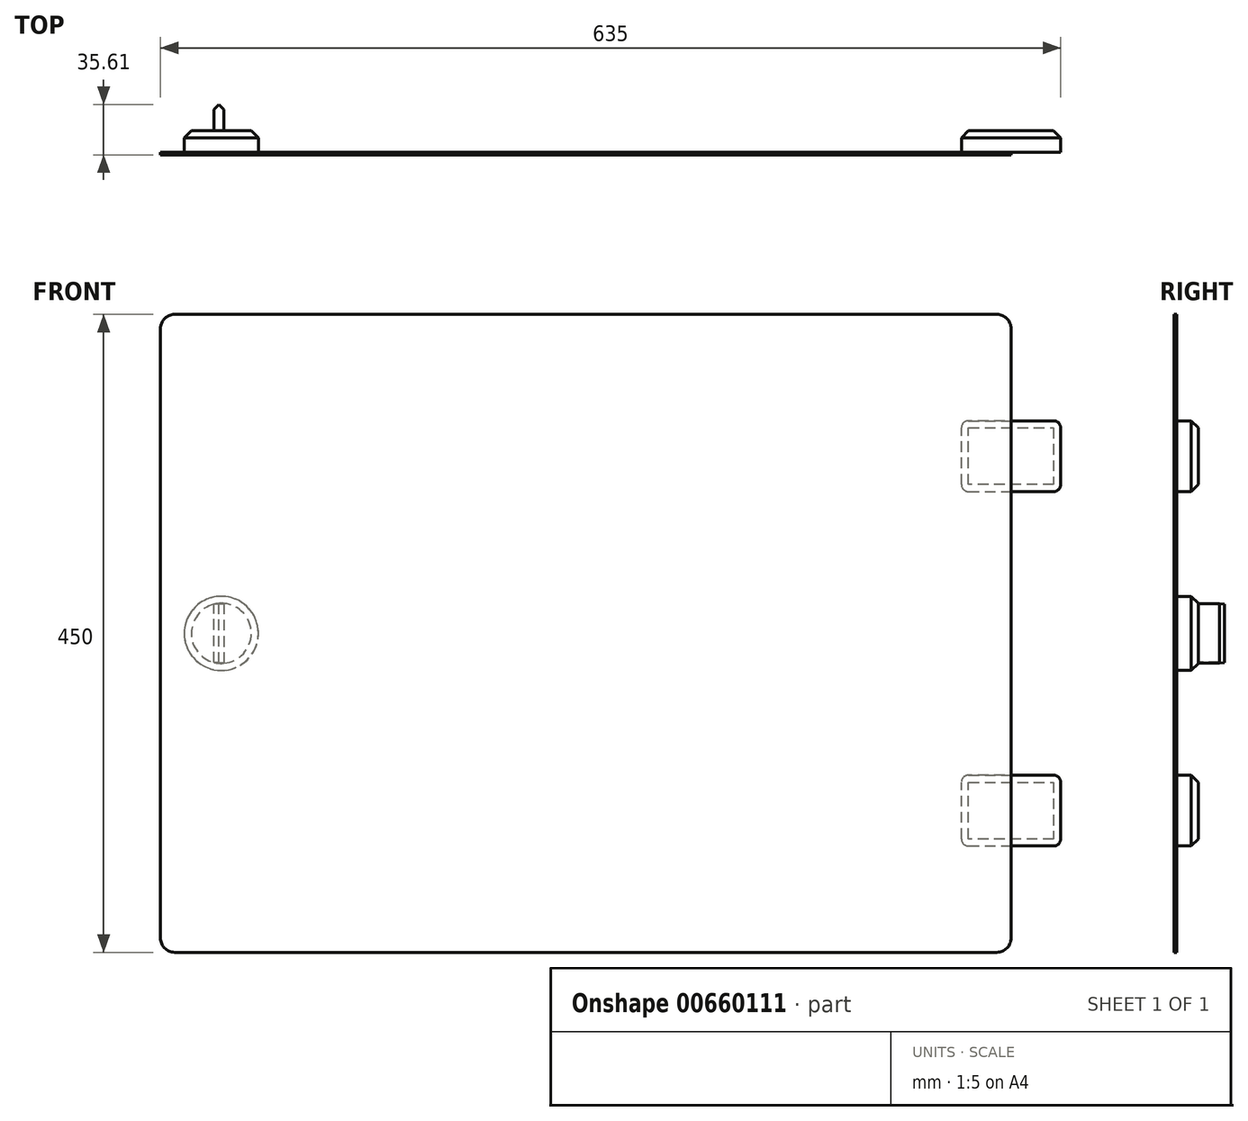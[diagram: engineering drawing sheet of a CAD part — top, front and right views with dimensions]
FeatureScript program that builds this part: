
annotation { "Feature Type Name" : "Feature", "Feature Type Description" : "" }
export const myFeature = defineFeature(function(context is Context, id is Id, definition is map)
    precondition{}
    {
        {
            var Q0;
            Q0=qCreatedBy(makeId("Front.planeOp"),FACE);
            var sketch = newSketch(context, id + "F0", { "sketchPlane" : qUnion([Q0])});
            skLineSegment(sketch, "E0.bottom", {"start": v(-290, -225) * mm, "end": v(290, -225) * mm});
            skLineSegment(sketch, "E0.top", {"start": v(-290, 225) * mm, "end": v(290, 225) * mm});
            skLineSegment(sketch, "E0.left", {"start": v(-300, -215) * mm, "end": v(-300, 215) * mm});
            skLineSegment(sketch, "E0.right", {"start": v(300, -215) * mm, "end": v(300, 215) * mm});
            skPoint(sketch, "E0.middle", {"position": v(0, 0) * mm});
            skPoint(sketch, "E1.visualSharp", {"position": v(-300, 225) * mm});
            skArc(sketch, "E1.filletArc", {"start": v(-290, 225) * mm, "mid": v(-297.07, 222.07) * mm, "end": v(-300, 215) * mm});
            skPoint(sketch, "E2.visualSharp", {"position": v(-300, -225) * mm});
            skArc(sketch, "E2.filletArc", {"start": v(-300, -215) * mm, "mid": v(-297.07, -222.07) * mm, "end": v(-290, -225) * mm});
            skPoint(sketch, "E3.visualSharp", {"position": v(300, -225) * mm});
            skArc(sketch, "E3.filletArc", {"start": v(290, -225) * mm, "mid": v(297.07, -222.07) * mm, "end": v(300, -215) * mm});
            skPoint(sketch, "E4.visualSharp", {"position": v(300, 225) * mm});
            skArc(sketch, "E4.filletArc", {"start": v(300, 215) * mm, "mid": v(297.07, 222.07) * mm, "end": v(290, 225) * mm});
            skSolve(sketch);
        }
        {
            var Q0;
            Q0 = qSketchRegion(id + "F0", true);
            extrude(context, id + "F1", {"entities" : qUnion([Q0]), "depth" : 2 * mm, "offsetDistance" : 25 * mm});
        }
        {
            var Q0;
            Q0=makeQuery(id+"F1.opExtrude","CAP_FACE",FACE,{"disambiguationData":[OSD([sQuery(id+"F0.wireOp",EDGE,"E0.bottom"),sQuery(id+"F0.wireOp",EDGE,"E0.top"),sQuery(id+"F0.wireOp",EDGE,"E0.left"),sQuery(id+"F0.wireOp",EDGE,"E0.right"),sQuery(id+"F0.wireOp",EDGE,"E1.filletArc"),sQuery(id+"F0.wireOp",EDGE,"E2.filletArc"),sQuery(id+"F0.wireOp",EDGE,"E3.filletArc"),sQuery(id+"F0.wireOp",EDGE,"E4.filletArc")])],"isStart":true});
            var sketch = newSketch(context, id + "F2", { "sketchPlane" : qUnion([Q0])});
            skCircle(sketch, "E5", {"center": v(257.08, 0) * mm, "radius": 26.15 * mm});
            skPoint(sketch, "E5.centerSnap0", {"position": v(300, 0) * mm});
            skLineSegment(sketch, "E6.bottom", {"start": v(-270, 100) * mm, "end": v(-330, 100) * mm});
            skLineSegment(sketch, "E6.top", {"start": v(-270, 150) * mm, "end": v(-330, 150) * mm});
            skLineSegment(sketch, "E6.left", {"start": v(-265, 105) * mm, "end": v(-265, 145) * mm});
            skLineSegment(sketch, "E6.right", {"start": v(-335, 105) * mm, "end": v(-335, 145) * mm});
            skPoint(sketch, "E6.middle", {"position": v(-300, 125) * mm});
            skLineSegment(sketch, "E7.bottom", {"start": v(-270, -150) * mm, "end": v(-330, -150) * mm});
            skLineSegment(sketch, "E7.top", {"start": v(-270, -100) * mm, "end": v(-330, -100) * mm});
            skLineSegment(sketch, "E7.left", {"start": v(-265, -145) * mm, "end": v(-265, -105) * mm});
            skLineSegment(sketch, "E7.right", {"start": v(-335, -145) * mm, "end": v(-335, -105) * mm});
            skPoint(sketch, "E7.middle", {"position": v(-300, -125) * mm});
            skPoint(sketch, "E8.visualSharp", {"position": v(-335, 150) * mm});
            skArc(sketch, "E8.filletArc", {"start": v(-330, 150) * mm, "mid": v(-333.54, 148.54) * mm, "end": v(-335, 145) * mm});
            skPoint(sketch, "E9.visualSharp", {"position": v(-335, 100) * mm});
            skArc(sketch, "E9.filletArc", {"start": v(-335, 105) * mm, "mid": v(-333.54, 101.46) * mm, "end": v(-330, 100) * mm});
            skPoint(sketch, "E10.visualSharp", {"position": v(-265, 100) * mm});
            skArc(sketch, "E10.filletArc", {"start": v(-270, 100) * mm, "mid": v(-266.46, 101.46) * mm, "end": v(-265, 105) * mm});
            skPoint(sketch, "E11.visualSharp", {"position": v(-265, 150) * mm});
            skArc(sketch, "E11.filletArc", {"start": v(-265, 145) * mm, "mid": v(-266.46, 148.54) * mm, "end": v(-270, 150) * mm});
            skPoint(sketch, "E12.visualSharp", {"position": v(-335, -100) * mm});
            skArc(sketch, "E12.filletArc", {"start": v(-330, -100) * mm, "mid": v(-333.54, -101.46) * mm, "end": v(-335, -105) * mm});
            skPoint(sketch, "E13.visualSharp", {"position": v(-335, -150) * mm});
            skArc(sketch, "E13.filletArc", {"start": v(-335, -145) * mm, "mid": v(-333.54, -148.54) * mm, "end": v(-330, -150) * mm});
            skPoint(sketch, "E14.visualSharp", {"position": v(-265, -150) * mm});
            skArc(sketch, "E14.filletArc", {"start": v(-270, -150) * mm, "mid": v(-266.46, -148.54) * mm, "end": v(-265, -145) * mm});
            skPoint(sketch, "E15.visualSharp", {"position": v(-265, -100) * mm});
            skArc(sketch, "E15.filletArc", {"start": v(-265, -105) * mm, "mid": v(-266.46, -101.46) * mm, "end": v(-270, -100) * mm});
            skSolve(sketch);
        }
        {
            var Q0;
            Q0 = qSketchRegion(id + "F2", true);
            extrude(context, id + "F3", {"entities" : qUnion([Q0]), "operationType" : NewBodyOperationType.ADD, "depth" : 15 * mm, "offsetDistance" : 25 * mm});
        }
        {
            var Q0;
            Q0=makeQuery(id+"F3.opExtrude","CAP_EDGE",EDGE,{"disambiguationData":[OSD([sQuery(id+"F2.wireOp",EDGE,"E5")])],"isStart":false});
            var Q1;
            Q1=makeQuery(id+"F3.opExtrude","CAP_EDGE",EDGE,{"disambiguationData":[OSD([sQuery(id+"F2.wireOp",EDGE,"E6.bottom")])],"isStart":false});
            var Q2;
            Q2=makeQuery(id+"F3.opExtrude","CAP_EDGE",EDGE,{"disambiguationData":[OSD([sQuery(id+"F2.wireOp",EDGE,"E7.bottom")])],"isStart":false});
            chamfer(context, id + "F4", {"entities" : qUnion([Q0, Q1, Q2]), "width" : 5 * mm, "tangentPropagation" : true});
        }
        {
            var Q0;
            Q0=makeQuery(id+"F3.opExtrude","CAP_FACE",FACE,{"disambiguationData":[OSD([sQuery(id+"F2.wireOp",EDGE,"E5")])],"isStart":false});
            var sketch = newSketch(context, id + "F5", { "sketchPlane" : qUnion([Q0])});
            skLineSegment(sketch, "E16", {"start": v(255.14, 21.06) * mm, "end": v(255.14, -21.06) * mm});
            skLineSegment(sketch, "E17", {"start": v(255.14, -21.06) * mm, "end": v(262.36, -20.49) * mm});
            skLineSegment(sketch, "E18", {"start": v(262.36, -20.49) * mm, "end": v(262.36, 20.49) * mm});
            skLineSegment(sketch, "E19", {"start": v(262.36, 20.49) * mm, "end": v(255.14, 21.06) * mm});
            skSolve(sketch);
        }
        {
            var Q0;
            Q0 = qSketchRegion(id + "F5", true);
            extrude(context, id + "F6", {"entities" : qUnion([Q0]), "operationType" : NewBodyOperationType.ADD, "depth" : 20 * mm, "offsetDistance" : 25 * mm});
        }
        {
            var Q0;
            Q0=makeQuery(id+"F6.opExtrude","CAP_EDGE",EDGE,{"disambiguationData":[OSD([sQuery(id+"F5.wireOp",EDGE,"E18")])],"isStart":false});
            var Q1;
            Q1=makeQuery(id+"F6.opExtrude","CAP_EDGE",EDGE,{"disambiguationData":[OSD([sQuery(id+"F5.wireOp",EDGE,"E16")])],"isStart":false});
            chamfer(context, id + "F7", {"entities" : qUnion([Q0, Q1]), "width" : 5 * mm, "tangentPropagation" : true});
        }
    });
